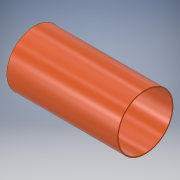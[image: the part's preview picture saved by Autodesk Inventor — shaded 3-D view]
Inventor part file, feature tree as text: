
AUTODESK INVENTOR PART (.ipt)
format: ipt  version: 2017 SP1 (Build 210196100, 196)  size: 108,544 bytes
history: native  units: in
note: dims shown in document units (in); Inventor stores cm internally (conversion verified against a paired STEP export)
features: extrude x1, sketch x1
ambient origin geometry x8: Origin, YZ Plane, XZ Plane, XY Plane, X Axis, Y Axis, Z Axis, Center Point
bodies: Solid1 (feature_tree)
feature tree (2):
  extrude  "Extrusion1"  Depth=14.2in
  sketch  "Sketch1"  dims[d0=7.15in d1=6.9in d2=14.2in d3=0.0in]
